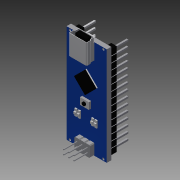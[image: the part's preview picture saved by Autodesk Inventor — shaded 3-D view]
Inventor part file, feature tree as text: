
AUTODESK INVENTOR PART (.ipt)
format: ipt  version: 2014 SP1 (Build 180222100, 222)  size: 745,472 bytes
history: native  units: mm
features: extrude x16, sketch x15, fillet x2, pattern_linear x1, mirror x1
ambient origin geometry x8: Origin, YZ Plane, XZ Plane, XY Plane, X Axis, Y Axis, Z Axis, Center Point
bodies: Solid1 (feature_tree)
feature tree (35):
  extrude  "Extrusion1"  Depth=44.0mm
  extrude  "Extrusion2"  Depth=2.5mm
  extrude  "Extrusion3"  Depth=1.5mm
  pattern_linear  "Rectangular Pattern1"  Count1=15 Spacing1=2.75mm
  mirror  "Mirror1"
  extrude  "Extrusion4"  Depth=1.5mm
  extrude  "Extrusion5"  Depth=6.0mm TaperAngle=0.0deg
  extrude  "Extrusion6"  Depth=5.0mm
  extrude  "Extrusion7"  TaperAngle=45.0deg  [1 undecoded]
  fillet  "Fillet1"  Radius=2.0mm
  extrude  "Extrusion8"  Depth=2.0mm
  fillet  "Fillet2"  Radius=2.0mm
  extrude  "Extrusion9"  Depth=0.5mm
  extrude  "Extrusion10"  Depth=0.5mm
  sketch  "Sketch11"  dims[d22=7.0mm d23=5.0mm]
  extrude  "Extrusion11"  Depth=0.5mm
  extrude  "Extrusion12"  Depth=1.5mm
  extrude  "Extrusion13"  Depth=1.5mm
  extrude  "Extrusion14"  Depth=6.0mm TaperAngle=0.0deg
  extrude  "Extrusion15"  Depth=7.0mm
  extrude  "Extrusion16"  Depth=2.0mm
  sketch  "Sketch1"  dims[d0=18.0mm d1=44.0mm]
  sketch  "Sketch2"  dims[d2=2.0mm d3=0.0mm d4=2.5mm]
  sketch  "Sketch3"  dims[d5=2.5mm d6=1.5mm]
  sketch  "Sketch4"  dims[d7=0.5mm]
  sketch  "Sketch5"  dims[d8=3.0mm d9=0.0mm]
  sketch  "Sketch6"  dims[d10=0.75mm]
  sketch  "Sketch7"  dims[d11=0.75mm]
  sketch  "Sketch8"  dims[d12=6.0mm d13=0.0mm d14=150.0mm d16=2.75mm]
  sketch  "Sketch9"  dims[d17=1.0mm d18=1.5mm]
  sketch  "Sketch10"  dims[d19=0.75mm d20=6.0mm d21=0.0mm]
  sketch  "Sketch13"  dims[d24=0.5mm d25=45.0deg d26=2.0mm]
  sketch  "Sketch14"  dims[d27=2.0mm d28=2.0mm d29=2.0mm]
  sketch  "Sketch15"  dims[d30=2.0mm d31=0.0mm d32=0.5mm]
  sketch  "Sketch16"  dims[d34=1.5mm d35=0.5mm d36=0.5mm d37=1.5mm d38=1.5mm d39=6.0mm d40=0.0mm d41=7.0mm d42=2.0mm d43=8.0mm d44=2.0mm d45=2.0mm d46=7.0mm d47=0.0mm d48=0.0mm d49=0.5mm d50=7.0mm d51=12.0mm d52=1.0mm d53=0.0mm d54=0.5mm d55=4.0mm d56=3.0mm d58=1.5mm d59=1.0mm d60=0.0mm d61=1.5mm d62=0.5mm d63=0.0mm d64=1.0mm d65=3.0mm d66=3.0mm d67=4.0mm d68=1.0mm d69=3.0mm d70=0.5mm d71=1.0mm d72=1.0mm d73=0.5mm d74=0.0mm d75=1.0mm d76=0.0mm d77=1.0mm d78=2.0mm d79=3.0mm d80=1.0mm d81=1.0mm d82=2.0mm d83=1.0mm d84=2.0mm d85=1.0mm d86=5.0mm d87=0.5mm d88=0.0mm d89=4.0mm d90=10.0mm d91=4.5mm d92=5.0mm d93=0.5mm d94=0.0mm d95=5.0mm d96=3.0mm d97=6.0mm d98=0.5mm d99=0.0mm d100=5.0mm d101=2.0mm d102=0.5mm d103=0.2mm d104=8.0mm d105=0.0mm]
note: 1 required parameter value undecoded (feature->parameter linkage not recoverable at this tier; creation-order binding heuristic only, values carry confidence <= 0.55)
